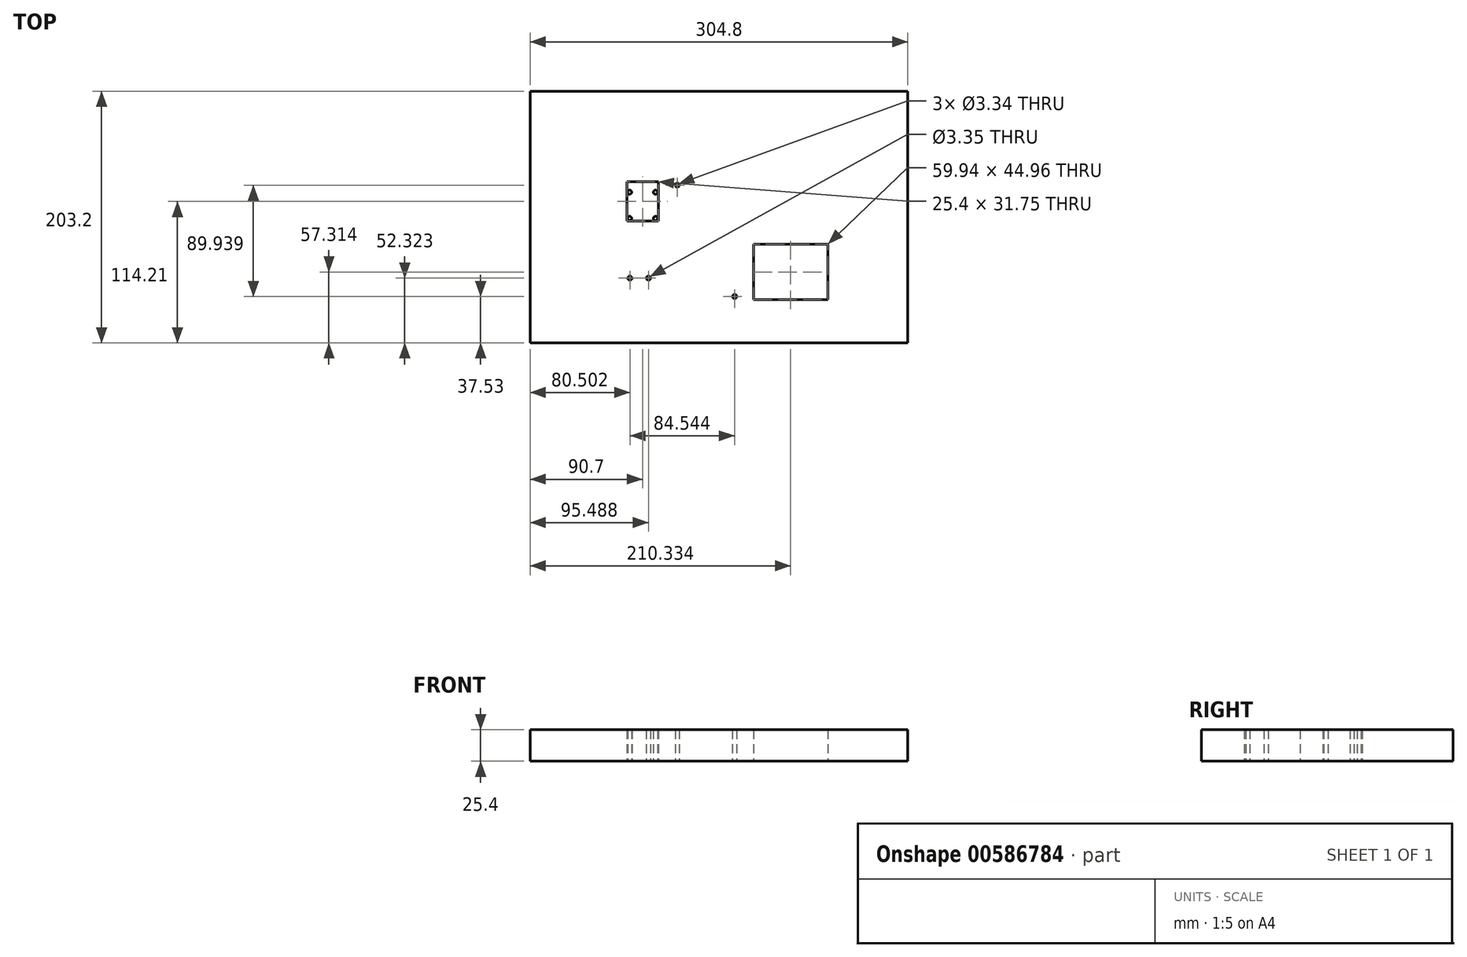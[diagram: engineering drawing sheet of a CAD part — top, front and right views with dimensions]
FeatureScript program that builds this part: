
annotation { "Feature Type Name" : "Feature", "Feature Type Description" : "" }
export const myFeature = defineFeature(function(context is Context, id is Id, definition is map)
    precondition{}
    {
        {
            var Q0;
            Q0=qCreatedBy(makeId("Top.planeOp"),FACE);
            var sketch = newSketch(context, id + "F0", { "sketchPlane" : qUnion([Q0])});
            skLineSegment(sketch, "E0.bottom", {"start": v(-174.3, 105.68) * mm, "end": v(130.5, 105.68) * mm});
            skLineSegment(sketch, "E0.top", {"start": v(-174.3, -97.52) * mm, "end": v(130.5, -97.52) * mm});
            skLineSegment(sketch, "E0.left", {"start": v(-174.3, 105.68) * mm, "end": v(-174.3, -97.52) * mm});
            skLineSegment(sketch, "E0.right", {"start": v(130.5, 105.68) * mm, "end": v(130.5, -97.52) * mm});
            skLineSegment(sketch, "E1.bottom", {"start": v(-96.3, -62.68) * mm, "end": v(-76.31, -62.68) * mm});
            skLineSegment(sketch, "E1.top", {"start": v(-96.3, -42.7) * mm, "end": v(-76.31, -42.7) * mm});
            skLineSegment(sketch, "E1.left", {"start": v(-96.3, -62.68) * mm, "end": v(-96.3, -42.7) * mm});
            skLineSegment(sketch, "E1.right", {"start": v(-76.31, -62.68) * mm, "end": v(-76.31, -42.7) * mm});
            skLineSegment(sketch, "E2.bottom", {"start": v(-96.3, 0.82) * mm, "end": v(-70.9, 0.82) * mm});
            skLineSegment(sketch, "E2.top", {"start": v(-96.3, 32.57) * mm, "end": v(-70.9, 32.57) * mm});
            skLineSegment(sketch, "E2.left", {"start": v(-96.3, 0.82) * mm, "end": v(-96.3, 32.57) * mm});
            skLineSegment(sketch, "E2.right", {"start": v(-70.9, 0.82) * mm, "end": v(-70.9, 32.57) * mm});
            skLineSegment(sketch, "E3.bottom", {"start": v(-58.2, -62.68) * mm, "end": v(-6.64, -62.68) * mm});
            skLineSegment(sketch, "E3.top", {"start": v(-58.2, 32.57) * mm, "end": v(-6.64, 32.57) * mm});
            skLineSegment(sketch, "E3.left", {"start": v(-58.2, -62.68) * mm, "end": v(-58.2, 32.57) * mm});
            skLineSegment(sketch, "E3.right", {"start": v(-6.64, -62.68) * mm, "end": v(-6.64, 32.57) * mm});
            skLineSegment(sketch, "E4.bottom", {"start": v(6.06, -62.68) * mm, "end": v(66, -62.68) * mm});
            skLineSegment(sketch, "E4.top", {"start": v(6.06, -17.73) * mm, "end": v(66, -17.73) * mm});
            skLineSegment(sketch, "E4.left", {"start": v(6.06, -62.68) * mm, "end": v(6.06, -17.73) * mm});
            skLineSegment(sketch, "E4.right", {"start": v(66, -62.68) * mm, "end": v(66, -17.73) * mm});
            skCircle(sketch, "E5", {"center": v(-55.58, -60.07) * mm, "radius": 1.67 * mm});
            skCircle(sketch, "E6", {"center": v(-93.8, -60.18) * mm, "radius": 1.67 * mm});
            skCircle(sketch, "E7", {"center": v(-78.81, -60.18) * mm, "radius": 1.68 * mm});
            skCircle(sketch, "E8.MirrorC", {"center": v(-78.81, -45.2) * mm, "radius": 1.68 * mm});
            skCircle(sketch, "E9.MirrorC", {"center": v(-93.8, -45.2) * mm, "radius": 1.67 * mm});
            skCircle(sketch, "E10.MirrorC", {"center": v(-9.25, -59.99) * mm, "radius": 1.67 * mm});
            skCircle(sketch, "E11.MirrorC", {"center": v(-9.25, 30.03) * mm, "radius": 1.67 * mm});
            skCircle(sketch, "E12.MirrorC", {"center": v(-55.58, 29.95) * mm, "radius": 1.67 * mm});
            skCircle(sketch, "E13", {"center": v(-94.06, 3.06) * mm, "radius": 1.67 * mm});
            skCircle(sketch, "E14", {"center": v(-73.14, 3.06) * mm, "radius": 1.67 * mm});
            skCircle(sketch, "E15", {"center": v(-94.06, 24.23) * mm, "radius": 1.67 * mm});
            skCircle(sketch, "E16", {"center": v(-73.14, 24.23) * mm, "radius": 1.67 * mm});
            skSolve(sketch);
        }
        {
            var Q0;
            Q0=makeQuery(id+"F0.imprint","IMPRINT",FACE,{"disambiguationData":[TD([[makeQuery(id+"F0.imprint","IMPRINT",EDGE,{"derivedFrom":sQuery(id+"F0.wireOp",EDGE,"E0.bottom")}),-1.0]])]});
            var Q1;
            Q1=makeQuery(id+"F0.imprint","IMPRINT",FACE,{"disambiguationData":[TD([[makeQuery(id+"F0.imprint","IMPRINT",EDGE,{"derivedFrom":sQuery(id+"F0.wireOp",EDGE,"E15")}),1.0]])]});
            var Q2;
            Q2=makeQuery(id+"F0.imprint","IMPRINT",FACE,{"disambiguationData":[TD([[makeQuery(id+"F0.imprint","IMPRINT",EDGE,{"derivedFrom":sQuery(id+"F0.wireOp",EDGE,"E16")}),1.0]])]});
            var Q3;
            Q3=makeQuery(id+"F0.imprint","IMPRINT",FACE,{"disambiguationData":[TD([[makeQuery(id+"F0.imprint","IMPRINT",EDGE,{"derivedFrom":sQuery(id+"F0.wireOp",EDGE,"E14")}),1.0]])]});
            var Q4;
            Q4=makeQuery(id+"F0.imprint","IMPRINT",FACE,{"disambiguationData":[TD([[makeQuery(id+"F0.imprint","IMPRINT",EDGE,{"derivedFrom":sQuery(id+"F0.wireOp",EDGE,"E13")}),1.0]])]});
            var Q5;
            Q5=makeQuery(id+"F0.imprint","IMPRINT",FACE,{"disambiguationData":[TD([[makeQuery(id+"F0.imprint","IMPRINT",EDGE,{"derivedFrom":sQuery(id+"F0.wireOp",EDGE,"E9.MirrorC")}),-1.0]])]});
            var Q6;
            Q6=makeQuery(id+"F0.imprint","IMPRINT",FACE,{"disambiguationData":[TD([[makeQuery(id+"F0.imprint","IMPRINT",EDGE,{"derivedFrom":sQuery(id+"F0.wireOp",EDGE,"E8.MirrorC")}),-1.0]])]});
            var Q7;
            Q7=makeQuery(id+"F0.imprint","IMPRINT",FACE,{"disambiguationData":[TD([[makeQuery(id+"F0.imprint","IMPRINT",EDGE,{"derivedFrom":sQuery(id+"F0.wireOp",EDGE,"E7")}),1.0]])]});
            var Q8;
            Q8=makeQuery(id+"F0.imprint","IMPRINT",FACE,{"disambiguationData":[TD([[makeQuery(id+"F0.imprint","IMPRINT",EDGE,{"derivedFrom":sQuery(id+"F0.wireOp",EDGE,"E6")}),1.0]])]});
            var Q9;
            Q9=makeQuery(id+"F0.imprint","IMPRINT",FACE,{"disambiguationData":[TD([[makeQuery(id+"F0.imprint","IMPRINT",EDGE,{"derivedFrom":sQuery(id+"F0.wireOp",EDGE,"E5")}),1.0]])]});
            var Q10;
            Q10=makeQuery(id+"F0.imprint","IMPRINT",FACE,{"disambiguationData":[TD([[makeQuery(id+"F0.imprint","IMPRINT",EDGE,{"derivedFrom":sQuery(id+"F0.wireOp",EDGE,"E12.MirrorC")}),-1.0]])]});
            var Q11;
            Q11=makeQuery(id+"F0.imprint","IMPRINT",FACE,{"disambiguationData":[TD([[makeQuery(id+"F0.imprint","IMPRINT",EDGE,{"derivedFrom":sQuery(id+"F0.wireOp",EDGE,"E11.MirrorC")}),1.0]])]});
            var Q12;
            Q12=makeQuery(id+"F0.imprint","IMPRINT",FACE,{"disambiguationData":[TD([[makeQuery(id+"F0.imprint","IMPRINT",EDGE,{"derivedFrom":sQuery(id+"F0.wireOp",EDGE,"E10.MirrorC")}),-1.0]])]});
            extrude(context, id + "F1", {"entities" : qUnion([Q0, Q1, Q2, Q3, Q4, Q5, Q6, Q7, Q8, Q9, Q10, Q11, Q12]), "depth" : 25.4 * mm, "offsetDistance" : 25.4 * mm});
        }
    });
